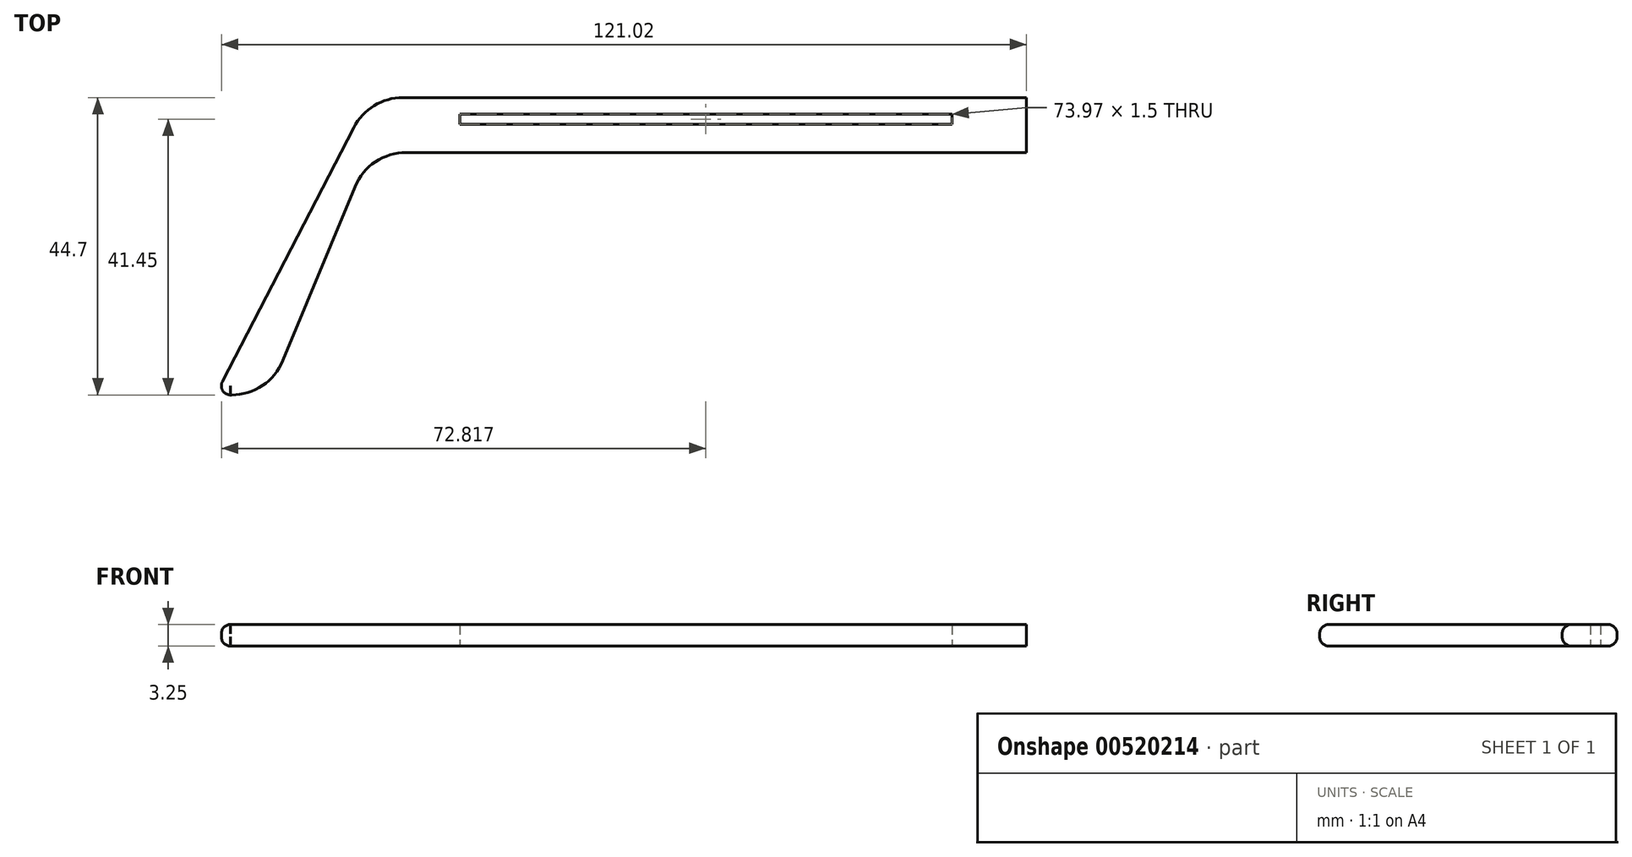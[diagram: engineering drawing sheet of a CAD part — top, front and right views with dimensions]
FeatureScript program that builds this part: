
annotation { "Feature Type Name" : "Feature", "Feature Type Description" : "" }
export const myFeature = defineFeature(function(context is Context, id is Id, definition is map)
    precondition{}
    {
        {
            var Q0;
            Q0=qCreatedBy(makeId("Top.planeOp"),FACE);
            var sketch = newSketch(context, id + "F0", { "sketchPlane" : qUnion([Q0])});
            skLineSegment(sketch, "E0", {"start": v(62.39, 8.25) * mm, "end": v(-31.33, 8.25) * mm});
            skLineSegment(sketch, "E1", {"start": v(-38.75, 3.73) * mm, "end": v(-59.51, -36.45) * mm});
            skLineSegment(sketch, "E2", {"start": v(-59.51, -36.45) * mm, "end": v(-57.1, -36.45) * mm});
            skLineSegment(sketch, "E3", {"start": v(-49.38, -31.3) * mm, "end": v(-38.55, -5.15) * mm});
            skLineSegment(sketch, "E4", {"start": v(-30.84, 0) * mm, "end": v(62.39, 0) * mm});
            skLineSegment(sketch, "E5", {"start": v(62.39, 0) * mm, "end": v(62.39, 8.25) * mm});
            skPoint(sketch, "E6.visualSharp", {"position": v(-36.41, 8.25) * mm});
            skArc(sketch, "E6.filletArc", {"start": v(-31.33, 8.25) * mm, "mid": v(-35.67, 7.03) * mm, "end": v(-38.75, 3.73) * mm});
            skPoint(sketch, "E7.visualSharp", {"position": v(-36.41, 0) * mm});
            skArc(sketch, "E7.filletArc", {"start": v(-30.84, 0) * mm, "mid": v(-35.47, -1.4) * mm, "end": v(-38.55, -5.15) * mm});
            skPoint(sketch, "E8.visualSharp", {"position": v(-51.51, -36.45) * mm});
            skArc(sketch, "E8.filletArc", {"start": v(-57.1, -36.45) * mm, "mid": v(-52.46, -35.04) * mm, "end": v(-49.38, -31.3) * mm});
            skLineSegment(sketch, "E9.bottom", {"start": v(51.17, 5.75) * mm, "end": v(-22.8, 5.75) * mm});
            skLineSegment(sketch, "E9.top", {"start": v(51.17, 4.25) * mm, "end": v(-22.8, 4.25) * mm});
            skLineSegment(sketch, "E9.left", {"start": v(51.17, 5.75) * mm, "end": v(51.17, 4.25) * mm});
            skLineSegment(sketch, "E9.right", {"start": v(-22.8, 5.75) * mm, "end": v(-22.8, 4.25) * mm});
            skSolve(sketch);
        }
        {
            var Q0;
            Q0=makeQuery(id+"F0.imprint","IMPRINT",FACE,{"disambiguationData":[TD([[makeQuery(id+"F0.imprint","IMPRINT",EDGE,{"derivedFrom":sQuery(id+"F0.wireOp",EDGE,"E0")}),1.0]])]});
            extrude(context, id + "F1", {"entities" : qUnion([Q0]), "depth" : 3.25 * mm, "offsetDistance" : 25 * mm});
        }
        {
            var Q0;
            Q0=makeQuery(id+"F1.opExtrude","CAP_EDGE",EDGE,{"disambiguationData":[OSD([sQuery(id+"F0.wireOp",EDGE,"E4")])],"isStart":false});
            fillet(context, id + "F2", {"entities" : qUnion([Q0]), "radius" : 2.75 / 2 * mm, "tangentPropagation" : true, "allowEdgeOverflow" : false});
        }
        {
            var Q0;
            Q0=makeQuery(id+"F1.opExtrude","CAP_EDGE",EDGE,{"disambiguationData":[OSD([sQuery(id+"F0.wireOp",EDGE,"E4")])],"isStart":true});
            fillet(context, id + "F3", {"entities" : qUnion([Q0]), "radius" : 2.75 / 2 * mm, "tangentPropagation" : true, "allowEdgeOverflow" : false});
        }
        {
            var Q0;
            Q0=makeQuery(id+"F1.opExtrude","CAP_EDGE",EDGE,{"disambiguationData":[OSD([sQuery(id+"F0.wireOp",EDGE,"E1")])],"isStart":true});
            var Q1;
            Q1=makeQuery(id+"F1.opExtrude","CAP_EDGE",EDGE,{"disambiguationData":[OSD([sQuery(id+"F0.wireOp",EDGE,"E1")])],"isStart":false});
            fillet(context, id + "F4", {"entities" : qUnion([Q0, Q1]), "radius" : 2.75 / 2 * mm, "tangentPropagation" : true, "allowEdgeOverflow" : false});
        }
    });
